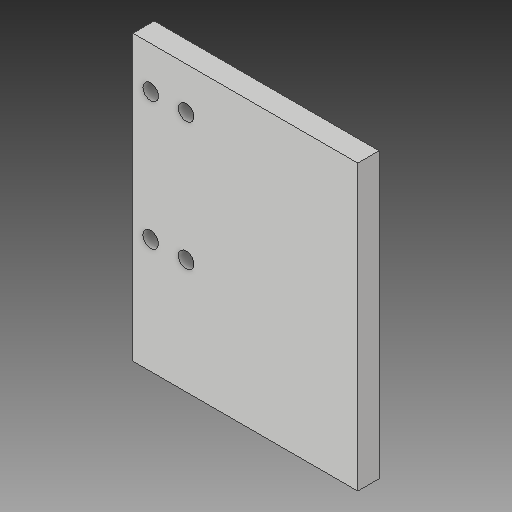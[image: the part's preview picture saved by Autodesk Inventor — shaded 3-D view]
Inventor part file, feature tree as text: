
AUTODESK INVENTOR PART (.ipt)
format: ipt  version: 2018 (Build 220112000, 112)  size: 114,688 bytes
history: native  units: mm
features: reference x4, extrude x3, sketch x3, fillet x1
ambient origin geometry x8: Origin, YZ Plane, XZ Plane, XY Plane, X Axis, Y Axis, Z Axis, Center Point
bodies: Solid1 (feature_tree)
feature tree (11):
  extrude  "Extrusion1"  Depth=95.0mm
  extrude  "Extrusion3"  Depth=7.0mm
  fillet  "Fillet1"  Radius=35.0mm
  extrude  "Extrusion4"  Depth=3.0mm TaperAngle=0.0deg
  sketch  "Sketch1"  dims[d0=120.0mm d1=95.0mm]
  sketch  "Sketch3"  dims[d2=6.0mm d3=0.0mm d9=7.0mm d10=35.0mm]
  sketch  "Sketch4"  dims[d11=75.0mm d12=3.0mm d13=0.0mm d14=7.0mm d15=10.0mm d16=0.0mm]
  reference  "Reference1"
  reference  "Reference2"
  reference  "Reference3"
  reference  "Reference4"
